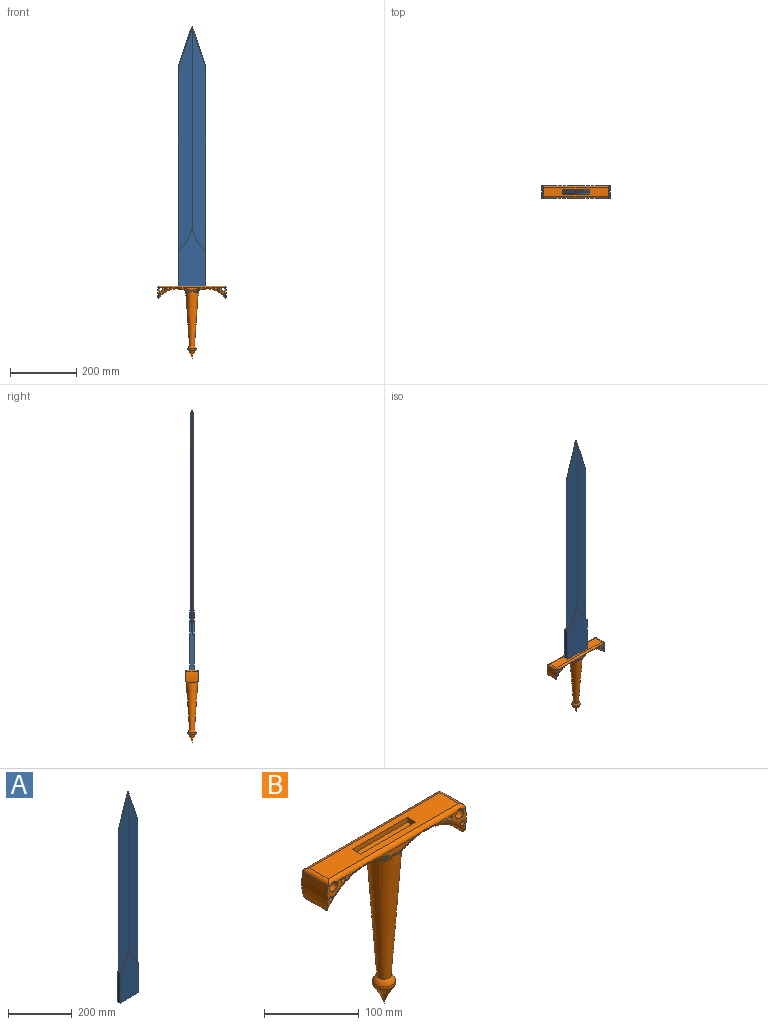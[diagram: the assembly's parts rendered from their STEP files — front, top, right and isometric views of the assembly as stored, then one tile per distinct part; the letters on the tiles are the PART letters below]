
ASSEMBLY  parts=2 mates=1
PART A: 19 faces, bbox 82.6x12.7x793.7 mm
  f0: plane 668.48x41.28mm, normal (0.1,-0.99,0), area 24306.3mm2, adj f1,f2,f7,f16
  f1: plane 668.48x41.28mm, normal (0.1,0.99,0), area 24306.3mm2, adj f0,f3,f12,f15
  f2: plane 668.48x41.28mm, normal (-0.1,-0.99,0), area 24306.3mm2, adj f0,f3,f6,f18
  f3: plane 668.48x41.28mm, normal (-0.1,0.99,0), area 24306.3mm2, adj f1,f2,f8,f17
  f4: plane 13.73x5.06mm, normal (0.94,0,0.35), area 7.8mm2, adj f5,f15,f16
  f5: plane 13.73x5.06mm, normal (-0.94,0,0.35), area 7.8mm2, adj f4,f17,f18
  f6: cylinder r=125.59mm len=73.64mm, axis (0,1,0), area 321.2mm2, adj f2,f7,f9,f13
  f7: cylinder r=125.59mm len=73.64mm, axis (0,1,0), area 321.2mm2, adj f0,f6,f11,f13
  f8: cylinder r=125.59mm len=73.64mm, axis (0,1,0), area 321.2mm2, adj f3,f9,f12,f14
  f9: plane 114.25x12.7mm, normal (-1,0,0), area 1451mm2, adj f6,f8,f10,f13,f14
  f10: plane 82.55x12.7mm, normal (0,0,-1), area 1048.4mm2, adj f9,f11,f13,f14
  f11: plane 114.25x12.7mm, normal (1,0,0), area 1451mm2, adj f7,f10,f12,f13,f14
  f12: cylinder r=125.59mm len=73.64mm, axis (0,1,0), area 321.2mm2, adj f1,f8,f11,f14
  f13: plane 187.88x82.55mm, normal (0,-1,0), area 11643.5mm2, adj f6,f7,f9,f10,f11
  f14: plane 187.88x82.55mm, normal (0,1,0), area 11643.5mm2, adj f8,f9,f10,f11,f12
  f15: plane 123.03x41.28mm, normal (0.7,0.67,0.23), area 378.7mm2, adj f1,f4,f16,f17
  f16: plane 123.03x41.28mm, normal (0.7,-0.67,0.23), area 378.7mm2, adj f0,f4,f15,f18
  f17: plane 123.03x41.28mm, normal (-0.7,0.67,0.23), area 378.7mm2, adj f3,f5,f15,f18
  f18: plane 123.03x41.28mm, normal (-0.7,-0.67,0.23), area 378.7mm2, adj f2,f5,f16,f17
PART B: 60 faces, bbox 228.1x38.2x223.6 mm
  f0: plane 194.99x27.94mm, normal (0,0,1), area 4399.7mm2, adj f49,f52,f53,f54,f55,f56,f57,f58
  f1: plane 41.89x26.29mm, normal (0,-1,0), area 268.4mm2, adj f13,f27,f31,f32,f47,f52
  f2: plane 41.89x26.29mm, normal (0,-1,0), area 268.4mm2, adj f14,f28,f29,f30,f48,f52
  f3: plane 41.89x26.29mm, normal (0,1,0), area 268.4mm2, adj f14,f28,f29,f30,f50,f53
  f4: plane 41.89x26.29mm, normal (0,1,0), area 268.4mm2, adj f13,f27,f31,f32,f51,f53
  f5: plane 52.8x7.45mm, normal (0,-1,0), area 219.2mm2, adj f33,f35,f36,f39,f40,f43,f44,f47
  f6: plane 52.8x7.45mm, normal (0,1,0), area 219.2mm2, adj f34,f37,f38,f41,f42,f45,f46,f50
  f7: torus R=73.76mm, axis (0,0,1), area 829.4mm2, adj f8
  f8: torus R=6.11mm, axis (0,0,1), area 432.4mm2, adj f7,f9
  f9: sphere r=12.7mm, area 536.6mm2, adj f8,f10
  f10: cone r=7.57mm half-angle=3.9deg, axis (0,0,1), area 13513.9mm2, adj f9,f15,f16,f17,f18,f19,f20,f21
  f11: cylinder r=69.82mm len=82.55mm, axis (0,1,0), area 2601.8mm2, adj f14,f18,f26,f48,f50
  f12: cylinder r=69.82mm len=82.55mm, axis (0,1,0), area 2601.8mm2, adj f13,f17,f21,f47,f51
  f13: cylinder r=80.94mm len=38.1mm, axis (0,1,0), area 1288.9mm2, adj f1,f4,f12,f47,f51,f52,f53,f54
  f14: cylinder r=80.94mm len=38.1mm, axis (0,1,0), area 1288.9mm2, adj f2,f3,f11,f48,f49,f50,f52,f53
  f15: bspline ~18.23x7.28mm, area 32.6mm2, adj f10,f16,f38
  f16: torus R=26.17mm, axis (0,0,1), area 8.9mm2, adj f10,f15,f17,f42
  f17: bspline ~18.25x7.28mm, area 77.1mm2, adj f10,f12,f16,f46
  f18: bspline ~18.25x7.28mm, area 77.1mm2, adj f10,f11,f19,f45
  f19: torus R=26.17mm, axis (0,0,1), area 8.9mm2, adj f10,f18,f20,f41
  f20: bspline ~18.23x7.28mm, area 32.6mm2, adj f10,f19,f37
  f21: bspline ~18.25x7.28mm, area 77.1mm2, adj f10,f12,f22,f43
  f22: torus R=26.17mm, axis (0,0,1), area 8.9mm2, adj f10,f21,f23,f39
  f23: bspline ~18.23x7.28mm, area 32.6mm2, adj f10,f22,f35
  f24: bspline ~18.23x7.28mm, area 32.6mm2, adj f10,f25,f36
  f25: torus R=26.17mm, axis (0,0,1), area 8.9mm2, adj f10,f24,f26,f40
  f26: bspline ~18.25x7.28mm, area 77.1mm2, adj f10,f11,f25,f44
  f27: cylinder r=5.81mm len=38.1mm, axis (0,-1,0), area 1391.4mm2, adj f1,f4,f52,f53
  f28: cylinder r=3.18mm len=38.1mm, axis (0,-1,0), area 760.1mm2, adj f2,f3,f48,f50
  f29: cylinder r=5.81mm len=38.1mm, axis (0,-1,0), area 1391.4mm2, adj f2,f3,f52,f53
  f30: cylinder r=3.12mm len=38.1mm, axis (0,-1,0), area 746.7mm2, adj f2,f3,f52,f53
  f31: cylinder r=3.18mm len=38.1mm, axis (0,-1,0), area 760.1mm2, adj f1,f4,f47,f51
  f32: cylinder r=3.12mm len=38.1mm, axis (0,-1,0), area 746.7mm2, adj f1,f4,f52,f53
  f33: bspline ~0.8x0.41mm, area 0.1mm2, adj f5,f10,f35,f36
  f34: bspline ~0.8x0.41mm, area 0.1mm2, adj f6,f10,f37,f38
  f35: bspline ~15.19x4.36mm, area 37.4mm2, adj f5,f23,f33,f39
  f36: bspline ~15.29x4.38mm, area 37.4mm2, adj f5,f24,f33,f40
  f37: bspline ~15.26x4.38mm, area 37.4mm2, adj f6,f20,f34,f41
  f38: bspline ~15.29x4.38mm, area 37.4mm2, adj f6,f15,f34,f42
  f39: bspline ~5.51x5.01mm, area 10mm2, adj f5,f22,f35,f43
  f40: bspline ~5.77x5.69mm, area 10mm2, adj f5,f25,f36,f44
  f41: bspline ~5.51x5.01mm, area 10mm2, adj f6,f19,f37,f45
  f42: bspline ~5.77x5.69mm, area 10mm2, adj f6,f16,f38,f46
  f43: bspline ~5.87x5.5mm, area 18.9mm2, adj f5,f21,f39,f47
  f44: bspline ~6.3x6.19mm, area 18.9mm2, adj f5,f26,f40,f48
  f45: bspline ~5.87x5.5mm, area 18.9mm2, adj f6,f18,f41,f50
  f46: bspline ~6.3x6.19mm, area 18.9mm2, adj f6,f17,f42,f51
  f47: torus R=74.9mm, axis (0,-1,0), area 714.1mm2, adj f1,f5,f12,f13,f31,f43,f52
  f48: torus R=74.9mm, axis (0,-1,0), area 714.1mm2, adj f2,f5,f11,f14,f28,f44,f52
  f49: cylinder r=5.08mm len=37.93mm, axis (0,1,0), area 231.8mm2, adj f0,f14,f52,f53
  f50: torus R=74.9mm, axis (0,-1,0), area 714.1mm2, adj f3,f6,f11,f14,f28,f45,f53
  f51: torus R=74.9mm, axis (0,-1,0), area 714.1mm2, adj f4,f6,f12,f13,f31,f46,f53
  f52: cylinder r=5.08mm len=205.32mm, axis (1,0,0), area 1534.3mm2, adj f0,f1,f2,f5,f13,f14,f27,f29
  f53: cylinder r=5.08mm len=205.32mm, axis (-1,0,0), area 1534.3mm2, adj f0,f3,f4,f6,f13,f14,f27,f29
  f54: cylinder r=5.08mm len=37.93mm, axis (0,1,0), area 231.8mm2, adj f0,f13,f52,f53
  f55: plane 82.55x6.35mm, normal (0,1,0), area 524.2mm2, adj f0,f56,f58,f59
  f56: plane 12.7x6.35mm, normal (-1,0,0), area 80.6mm2, adj f0,f55,f57,f59
  f57: plane 82.55x6.35mm, normal (0,-1,0), area 524.2mm2, adj f0,f56,f58,f59
  f58: plane 12.7x6.35mm, normal (1,0,0), area 80.6mm2, adj f0,f55,f57,f59
  f59: plane 82.55x12.7mm, normal (0,0,1), area 1048.4mm2, adj f55,f56,f57,f58
PLACE A t=(-40.67,9.73,174.38)mm
PLACE B t=(-40.67,9.73,-12.16)mm
MATE slider A.f10 <-> B.f7  axis (0,0,-1) through (-40.67,9.73,149.03)mm
